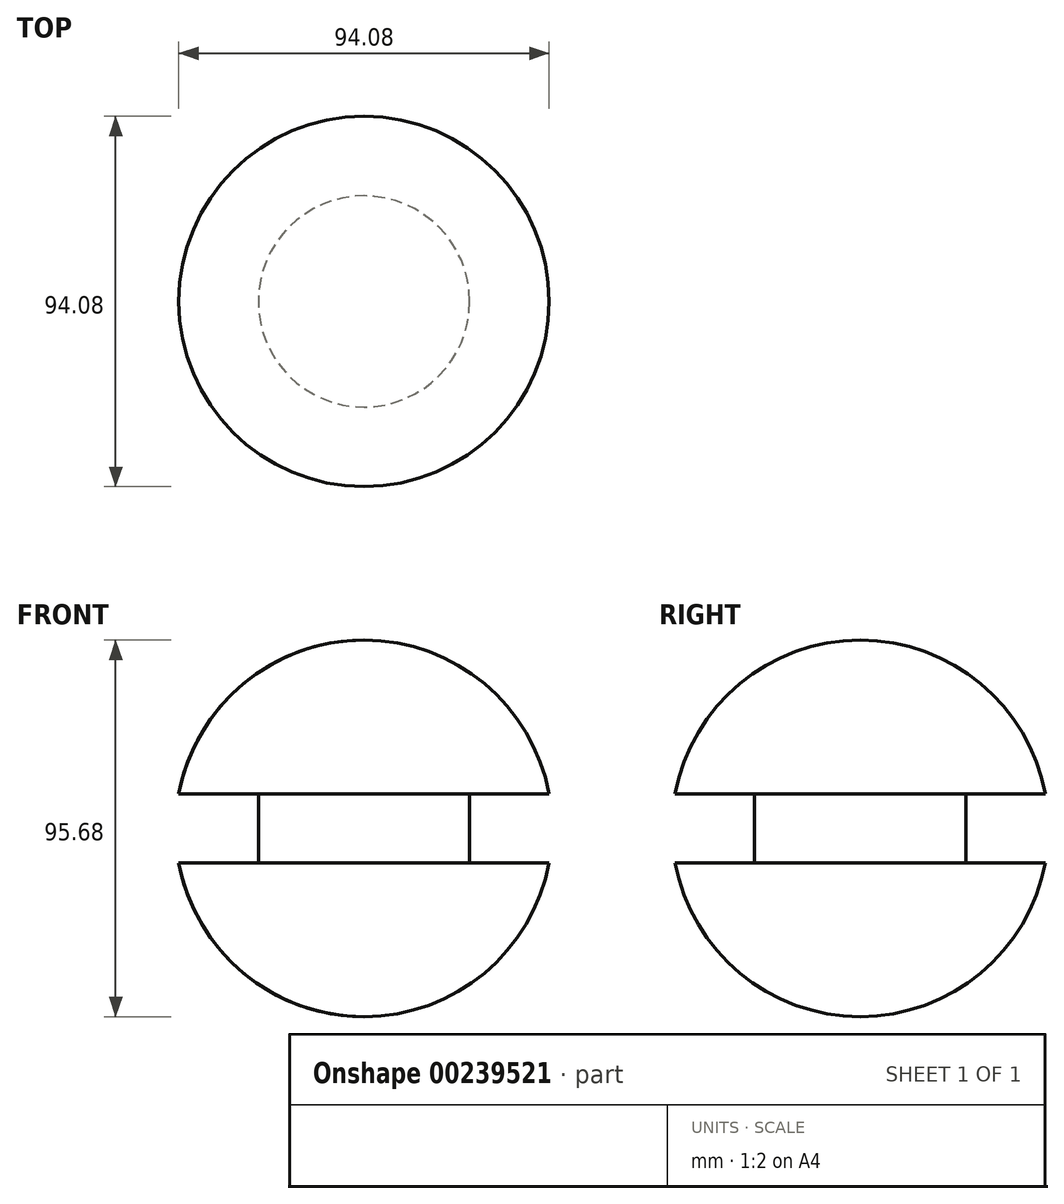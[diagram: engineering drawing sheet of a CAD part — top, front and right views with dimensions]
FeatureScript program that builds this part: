
annotation { "Feature Type Name" : "Feature", "Feature Type Description" : "" }
export const myFeature = defineFeature(function(context is Context, id is Id, definition is map)
    precondition{}
    {
        {
            var Q0;
            Q0=qCreatedBy(makeId("Front.planeOp"),FACE);
            var sketch = newSketch(context, id + "F0", { "sketchPlane" : qUnion([Q0])});
            skArc(sketch, "E0", {"start": v(0, -47.84) * mm, "mid": v(47.84, 0) * mm, "end": v(0, 47.84) * mm});
            skLineSegment(sketch, "E1", {"start": v(0, 47.84) * mm, "end": v(0, -47.84) * mm});
            skSolve(sketch);
        }
        {
            var Q0;
            Q0 = qSketchRegion(id + "F0", true);
            var Q1;
            Q1=sQuery(id+"F0.wireOp",EDGE,"E1");
            revolve(context, id + "F1", {"entities" : qUnion([Q0]), "axis" : qUnion([Q1]), "revolveType" : RevolveType.FULL});
        }
        {
            var Q0;
            Q0=qCreatedBy(makeId("Front.planeOp"),FACE);
            var sketch = newSketch(context, id + "F2", { "sketchPlane" : qUnion([Q0])});
            skLineSegment(sketch, "E2.bottom", {"start": v(26.83, 8.72) * mm, "end": v(55.43, 8.72) * mm});
            skLineSegment(sketch, "E2.top", {"start": v(26.83, -8.72) * mm, "end": v(55.43, -8.72) * mm});
            skLineSegment(sketch, "E2.left", {"start": v(26.83, 8.72) * mm, "end": v(26.83, -8.72) * mm});
            skLineSegment(sketch, "E2.right", {"start": v(55.43, 8.72) * mm, "end": v(55.43, -8.72) * mm});
            skLineSegment(sketch, "E3", {"start": v(0, 48.08) * mm, "end": v(0, -47.5) * mm});
            skSolve(sketch);
        }
        {
            var Q0;
            Q0 = qSketchRegion(id + "F2", true);
            var Q1;
            Q1=sQuery(id+"F2.wireOp",EDGE,"E3");
            revolve(context, id + "F3", {"operationType" : NewBodyOperationType.REMOVE, "entities" : qUnion([Q0]), "axis" : qUnion([Q1]), "revolveType" : RevolveType.FULL, "oppositeDirection" : true});
        }
    });
